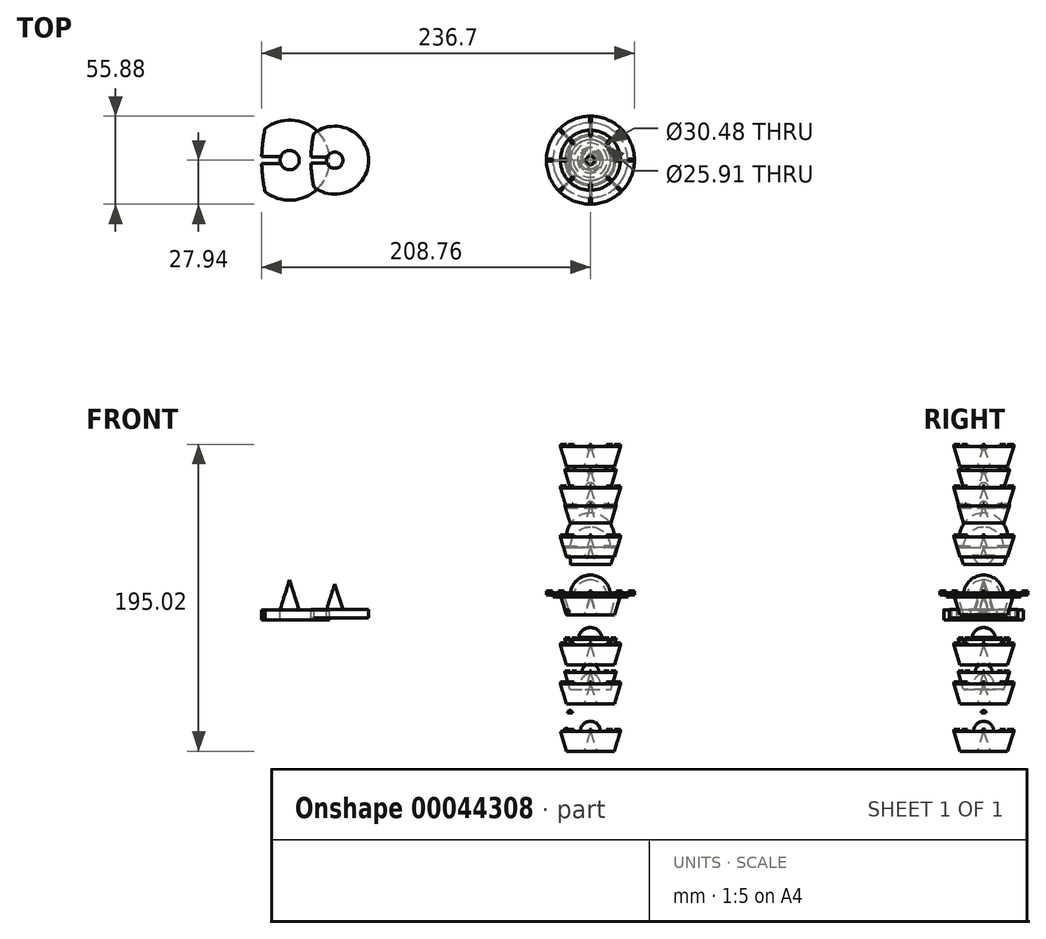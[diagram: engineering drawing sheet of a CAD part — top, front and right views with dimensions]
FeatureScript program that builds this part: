
annotation { "Feature Type Name" : "Feature", "Feature Type Description" : "" }
export const myFeature = defineFeature(function(context is Context, id is Id, definition is map)
    precondition{}
    {
        {
            var Q0;
            Q0=qCreatedBy(makeId("Front.planeOp"),FACE);
            var sketch = newSketch(context, id + "F0", { "sketchPlane" : qUnion([Q0])});
            skLineSegment(sketch, "E0", {"start": v(-19.05, 76.2) * mm, "end": v(0, 76.2) * mm});
            skLineSegment(sketch, "E1", {"start": v(0, 76.2) * mm, "end": v(0, 76.2) * mm});
            skLineSegment(sketch, "E2", {"start": v(-15.24, 63.5) * mm, "end": v(-19.05, 76.2) * mm});
            skLineSegment(sketch, "E3", {"start": v(-15.24, 63.5) * mm, "end": v(-4.06, 63.5) * mm});
            skLineSegment(sketch, "E4", {"start": v(0, 76.2) * mm, "end": v(-4.06, 63.5) * mm});
            skLineSegment(sketch, "E5", {"start": v(-15.24, 63.5) * mm, "end": v(-15.24, 76.2) * mm});
            skLineSegment(sketch, "E6", {"start": v(0, 76.2) * mm, "end": v(0, 79.38) * mm});
            skArc(sketch, "E7", {"start": v(0, 79.38) * mm, "mid": v(-2.25, 78.45) * mm, "end": v(-3.18, 76.2) * mm});
            skSolve(sketch);
        }
        {
            var Q0;
            Q0 = qSketchRegion(id + "F0", true);
            var Q1;
            Q1=sQuery(id+"F0.wireOp",EDGE,"E6");
            revolve(context, id + "F1", {"entities" : qUnion([Q0]), "axis" : qUnion([Q1]), "revolveType" : RevolveType.FULL});
        }
        {
            var Q0;
            Q0=qCreatedBy(makeId("Front.planeOp"),FACE);
            var sketch = newSketch(context, id + "F2", { "sketchPlane" : qUnion([Q0])});
            skLineSegment(sketch, "E8.top", {"start": v(-215.84, 27.03) * mm, "end": v(-190.44, 27.03) * mm});
            skLineSegment(sketch, "E8.left", {"start": v(-215.84, 33.38) * mm, "end": v(-215.84, 27.03) * mm});
            skLineSegment(sketch, "E9", {"start": v(-215.84, 33.38) * mm, "end": v(-190.44, 33.38) * mm});
            skLineSegment(sketch, "E10", {"start": v(-190.44, 33.38) * mm, "end": v(-190.44, 27.03) * mm});
            skLineSegment(sketch, "E11", {"start": v(-190.44, 33.38) * mm, "end": v(-196.53, 33.38) * mm});
            skLineSegment(sketch, "E12", {"start": v(-196.53, 33.38) * mm, "end": v(-190.44, 52.43) * mm});
            skLineSegment(sketch, "E13", {"start": v(-190.44, 52.43) * mm, "end": v(-190.44, 33.38) * mm});
            skSolve(sketch);
        }
        {
            var Q0;
            Q0 = qSketchRegion(id + "F2", true);
            var Q1;
            Q1=sQuery(id+"F2.wireOp",EDGE,"E10");
            revolve(context, id + "F3", {"entities" : qUnion([Q0]), "axis" : qUnion([Q1]), "revolveType" : RevolveType.FULL});
        }
        {
            var Q0;
            Q0=qCreatedBy(makeId("Front.planeOp"),FACE);
            var sketch = newSketch(context, id + "F4", { "sketchPlane" : qUnion([Q0])});
            skLineSegment(sketch, "E14.bottom", {"start": v(-216.4, -1.22) * mm, "end": v(-191, -1.22) * mm});
            skLineSegment(sketch, "E14.top", {"start": v(-216.4, -7.57) * mm, "end": v(-191, -7.57) * mm});
            skLineSegment(sketch, "E14.left", {"start": v(-216.4, -1.22) * mm, "end": v(-216.4, -7.57) * mm});
            skLineSegment(sketch, "E14.right", {"start": v(-191, -1.22) * mm, "end": v(-191, -7.57) * mm});
            skLineSegment(sketch, "E15", {"start": v(-191, -1.22) * mm, "end": v(-191, 17.83) * mm});
            skLineSegment(sketch, "E16", {"start": v(-191, 17.83) * mm, "end": v(-197.1, -1.22) * mm});
            skSolve(sketch);
        }
        {
            var Q0;
            Q0 = qSketchRegion(id + "F4", true);
            var Q1;
            Q1=sQuery(id+"F4.wireOp",EDGE,"E14.right");
            revolve(context, id + "F5", {"entities" : qUnion([Q0]), "axis" : qUnion([Q1]), "revolveType" : RevolveType.FULL});
        }
        {
            var Q0;
            Q0=makeQuery(id+"F3.opRevolve","SWEPT_FACE",FACE,{"disambiguationData":[OSD([sQuery(id+"F2.wireOp",EDGE,"E9")])]});
            var sketch = newSketch(context, id + "F6", { "sketchPlane" : qUnion([Q0])});
            skCircle(sketch, "E17", {"center": v(-114.24, 0) * mm, "radius": 101.6 * mm});
            skCircle(sketch, "E18", {"center": v(-114.24, 0) * mm, "radius": 93.98 * mm});
            skLineSegment(sketch, "E19", {"start": v(-114.24, 0) * mm, "end": v(-201.87, 0) * mm});
            skLineSegment(sketch, "E20.bottom", {"start": v(-214.57, 3.81) * mm, "end": v(-201.87, 3.81) * mm});
            skLineSegment(sketch, "E20.top", {"start": v(-214.57, -3.81) * mm, "end": v(-201.87, -3.81) * mm});
            skLineSegment(sketch, "E20.left", {"start": v(-214.57, 3.81) * mm, "end": v(-214.57, -3.81) * mm});
            skLineSegment(sketch, "E20.right", {"start": v(-201.87, 3.81) * mm, "end": v(-201.87, -3.81) * mm});
            skSolve(sketch);
        }
        {
            var Q0;
            Q0 = qSketchRegion(id + "F6", true);
            var Q1;
            {var subQ4=sQuery(id+"F6.wireOp",EDGE,"E18");var subQ6=sQuery(id+"F6.wireOp",EDGE,"E20.bottom");var subQ7=makeQuery(id+"F6.imprint","INTERSECT",VERTEX,{"derivedFrom":[subQ4,subQ6]});Q1=makeQuery(id+"F6.imprint","IMPRINT",FACE,{"disambiguationData":[TD([[makeQuery(id+"F6.imprint","IMPRINT",EDGE,{"disambiguationData":[TD([[subQ7,-1.0]])],"derivedFrom":subQ4}),1.0]])]});}
            var Q2;
            Q2=makeQuery(id+"F3.opRevolve","SWEPT_FACE",FACE,{"disambiguationData":[OSD([sQuery(id+"F2.wireOp",EDGE,"E8.top")])]});
            extrude(context, id + "F7", {"entities" : qUnion([Q0, Q1]), "operationType" : NewBodyOperationType.REMOVE, "endBound" : BoundingType.UP_TO_SURFACE, "oppositeDirection" : true, "endBoundEntityFace" : qUnion([Q2]), "depth" : 25.4 * mm});
        }
        {
            var Q0;
            Q0=makeQuery(id+"F5.opRevolve","SWEPT_FACE",FACE,{"disambiguationData":[OSD([sQuery(id+"F4.wireOp",EDGE,"E14.bottom")])]});
            var sketch = newSketch(context, id + "F8", { "sketchPlane" : qUnion([Q0])});
            skCircle(sketch, "E21", {"center": v(-114.8, 0) * mm, "radius": 101.6 * mm});
            skCircle(sketch, "E22", {"center": v(-114.8, 0) * mm, "radius": 93.98 * mm});
            skLineSegment(sketch, "E23", {"start": v(-114.8, 0) * mm, "end": v(-197.1, 0) * mm});
            skLineSegment(sketch, "E24.bottom", {"start": v(-214.88, 2.22) * mm, "end": v(-197.1, 2.22) * mm});
            skLineSegment(sketch, "E24.top", {"start": v(-214.88, -2.22) * mm, "end": v(-197.1, -2.22) * mm});
            skLineSegment(sketch, "E24.left", {"start": v(-214.88, 2.22) * mm, "end": v(-214.88, -2.22) * mm});
            skLineSegment(sketch, "E24.right", {"start": v(-197.1, 2.22) * mm, "end": v(-197.1, -2.22) * mm});
            skSolve(sketch);
        }
        {
            var Q0;
            Q0 = qSketchRegion(id + "F8", true);
            var Q1;
            {var subQ4=sQuery(id+"F8.wireOp",EDGE,"E22");var subQ6=sQuery(id+"F8.wireOp",EDGE,"E24.bottom");var subQ7=makeQuery(id+"F8.imprint","INTERSECT",VERTEX,{"derivedFrom":[subQ4,subQ6]});Q1=makeQuery(id+"F8.imprint","IMPRINT",FACE,{"disambiguationData":[TD([[makeQuery(id+"F8.imprint","IMPRINT",EDGE,{"disambiguationData":[TD([[subQ7,-1.0]])],"derivedFrom":subQ4}),1.0]])]});}
            var Q2;
            {var subQ0=sQuery(id+"F8.wireOp",EDGE,"E24.left");Q2=makeQuery(id+"F8.imprint","IMPRINT",FACE,{"disambiguationData":[TD([[makeQuery(id+"F8.imprint","IMPRINT",EDGE,{"derivedFrom":subQ0}),1.0]])]});}
            var Q3;
            Q3=makeQuery(id+"F5.opRevolve","SWEPT_FACE",FACE,{"disambiguationData":[OSD([sQuery(id+"F4.wireOp",EDGE,"E14.top")])]});
            extrude(context, id + "F9", {"entities" : qUnion([Q0, Q1, Q2]), "operationType" : NewBodyOperationType.REMOVE, "endBound" : BoundingType.UP_TO_SURFACE, "oppositeDirection" : true, "endBoundEntityFace" : qUnion([Q3]), "depth" : 25.4 * mm});
        }
        {
            var Q0;
            Q0=qCreatedBy(makeId("Front.planeOp"),FACE);
            var sketch = newSketch(context, id + "F10", { "sketchPlane" : qUnion([Q0])});
            skLineSegment(sketch, "E25", {"start": v(-19.05, 44.92) * mm, "end": v(0, 44.92) * mm});
            skLineSegment(sketch, "E26", {"start": v(0, 44.92) * mm, "end": v(0, 44.92) * mm});
            skLineSegment(sketch, "E27", {"start": v(0, 44.92) * mm, "end": v(-4.06, 32.22) * mm});
            skLineSegment(sketch, "E28", {"start": v(-4.06, 32.22) * mm, "end": v(-15.24, 32.22) * mm});
            skLineSegment(sketch, "E29", {"start": v(-15.24, 32.22) * mm, "end": v(-19.05, 44.92) * mm});
            skLineSegment(sketch, "E30", {"start": v(-15.24, 32.22) * mm, "end": v(-15.24, 44.92) * mm});
            skLineSegment(sketch, "E31", {"start": v(0, 44.92) * mm, "end": v(0, 60.16) * mm});
            skArc(sketch, "E32", {"start": v(0, 60.16) * mm, "mid": v(-10.78, 55.7) * mm, "end": v(-15.24, 44.92) * mm});
            skSolve(sketch);
        }
        {
            var Q0;
            Q0 = qSketchRegion(id + "F10", true);
            var Q1;
            Q1=sQuery(id+"F10.wireOp",EDGE,"E31");
            revolve(context, id + "F11", {"entities" : qUnion([Q0]), "axis" : qUnion([Q1]), "revolveType" : RevolveType.FULL});
        }
        {
            var Q0;
            Q0=qCreatedBy(makeId("Front.planeOp"),FACE);
            var sketch = newSketch(context, id + "F12", { "sketchPlane" : qUnion([Q0])});
            skLineSegment(sketch, "E33", {"start": v(-19.05, 8.07) * mm, "end": v(0, 8.07) * mm});
            skLineSegment(sketch, "E34", {"start": v(0, 8.07) * mm, "end": v(0, 8.07) * mm});
            skLineSegment(sketch, "E35", {"start": v(0, 8.07) * mm, "end": v(-4.06, -4.63) * mm});
            skLineSegment(sketch, "E36", {"start": v(-4.06, -4.63) * mm, "end": v(-15.24, -4.63) * mm});
            skLineSegment(sketch, "E37", {"start": v(-15.24, -4.63) * mm, "end": v(-19.05, 8.07) * mm});
            skLineSegment(sketch, "E38", {"start": v(-15.24, -4.63) * mm, "end": v(-15.24, 8.07) * mm});
            skLineSegment(sketch, "E39", {"start": v(0, 8.07) * mm, "end": v(0, 20.77) * mm});
            skArc(sketch, "E40", {"start": v(0, 20.77) * mm, "mid": v(-8.98, 17.05) * mm, "end": v(-12.7, 8.07) * mm});
            skSolve(sketch);
        }
        {
            var Q0;
            Q0 = qSketchRegion(id + "F12", true);
            var Q1;
            Q1=sQuery(id+"F12.wireOp",EDGE,"E39");
            revolve(context, id + "F13", {"entities" : qUnion([Q0]), "axis" : qUnion([Q1]), "revolveType" : RevolveType.FULL});
        }
        {
            var Q0;
            Q0=qCreatedBy(makeId("Front.planeOp"),FACE);
            var sketch = newSketch(context, id + "F14", { "sketchPlane" : qUnion([Q0])});
            skLineSegment(sketch, "E41.bottom", {"start": v(-27.94, 9.34) * mm, "end": v(-15.24, 9.34) * mm});
            skLineSegment(sketch, "E41.top", {"start": v(-27.94, 8.07) * mm, "end": v(-15.24, 8.07) * mm});
            skLineSegment(sketch, "E41.left", {"start": v(-27.94, 9.34) * mm, "end": v(-27.94, 8.07) * mm});
            skLineSegment(sketch, "E41.right", {"start": v(-15.24, 9.34) * mm, "end": v(-15.24, 8.07) * mm});
            skSolve(sketch);
        }
        {
            var Q0;
            Q0 = qSketchRegion(id + "F14", true);
            var Q1;
            Q1=sQuery(id+"F12.wireOp",EDGE,"E39");
            revolve(context, id + "F15", {"entities" : qUnion([Q0]), "axis" : qUnion([Q1]), "revolveType" : RevolveType.FULL});
        }
        {
            var Q0;
            Q0=qCreatedBy(makeId("Front.planeOp"),FACE);
            var sketch = newSketch(context, id + "F16", { "sketchPlane" : qUnion([Q0])});
            skLineSegment(sketch, "E42", {"start": v(-19.05, -23.63) * mm, "end": v(0, -23.63) * mm});
            skLineSegment(sketch, "E43", {"start": v(0, -23.63) * mm, "end": v(0, -23.63) * mm});
            skLineSegment(sketch, "E44", {"start": v(0, -23.63) * mm, "end": v(-4.06, -36.33) * mm});
            skLineSegment(sketch, "E45", {"start": v(-4.06, -36.33) * mm, "end": v(-15.24, -36.33) * mm});
            skLineSegment(sketch, "E46", {"start": v(-15.24, -36.33) * mm, "end": v(-19.05, -23.63) * mm});
            skLineSegment(sketch, "E47", {"start": v(-15.24, -36.33) * mm, "end": v(-15.24, -23.63) * mm});
            skLineSegment(sketch, "E48", {"start": v(0, -23.63) * mm, "end": v(0, -14.74) * mm});
            skArc(sketch, "E49", {"start": v(0, -14.74) * mm, "mid": v(-6.29, -17.34) * mm, "end": v(-8.9, -23.63) * mm});
            skSolve(sketch);
        }
        {
            var Q0;
            Q0 = qSketchRegion(id + "F16", true);
            var Q1;
            Q1=sQuery(id+"F16.wireOp",EDGE,"E48");
            revolve(context, id + "F17", {"entities" : qUnion([Q0]), "axis" : qUnion([Q1]), "revolveType" : RevolveType.FULL});
        }
        {
            var Q0;
            Q0=qCreatedBy(makeId("Front.planeOp"),FACE);
            var sketch = newSketch(context, id + "F18", { "sketchPlane" : qUnion([Q0])});
            skLineSegment(sketch, "E50", {"start": v(-19.05, -48.33) * mm, "end": v(0, -48.33) * mm});
            skLineSegment(sketch, "E51", {"start": v(0, -48.33) * mm, "end": v(0, -48.33) * mm});
            skLineSegment(sketch, "E52", {"start": v(0, -48.33) * mm, "end": v(-4.06, -61.03) * mm});
            skLineSegment(sketch, "E53", {"start": v(-4.06, -61.03) * mm, "end": v(-15.24, -61.03) * mm});
            skLineSegment(sketch, "E54", {"start": v(-15.24, -61.03) * mm, "end": v(-19.05, -48.33) * mm});
            skLineSegment(sketch, "E55", {"start": v(-15.24, -61.03) * mm, "end": v(-15.24, -48.33) * mm});
            skLineSegment(sketch, "E56", {"start": v(0, -48.33) * mm, "end": v(0, -41.98) * mm});
            skArc(sketch, "E57", {"start": v(0, -41.98) * mm, "mid": v(-4.5, -43.84) * mm, "end": v(-6.35, -48.33) * mm});
            skSolve(sketch);
        }
        {
            var Q0;
            Q0 = qSketchRegion(id + "F18", true);
            var Q1;
            Q1=sQuery(id+"F18.wireOp",EDGE,"E56");
            revolve(context, id + "F19", {"entities" : qUnion([Q0]), "axis" : qUnion([Q1]), "revolveType" : RevolveType.FULL});
        }
        {
            var Q0;
            Q0=qCreatedBy(makeId("Front.planeOp"),FACE);
            var sketch = newSketch(context, id + "F20", { "sketchPlane" : qUnion([Q0])});
            skLineSegment(sketch, "E58", {"start": v(-19.05, -78.45) * mm, "end": v(0, -78.45) * mm});
            skLineSegment(sketch, "E59", {"start": v(0, -78.45) * mm, "end": v(0, -78.45) * mm});
            skLineSegment(sketch, "E60", {"start": v(0, -78.45) * mm, "end": v(-4.06, -91.15) * mm});
            skLineSegment(sketch, "E61", {"start": v(-4.06, -91.15) * mm, "end": v(-15.24, -91.15) * mm});
            skLineSegment(sketch, "E62", {"start": v(-15.24, -91.15) * mm, "end": v(-19.05, -78.45) * mm});
            skLineSegment(sketch, "E63", {"start": v(-15.24, -91.15) * mm, "end": v(-15.24, -78.45) * mm});
            skLineSegment(sketch, "E64", {"start": v(0, -78.45) * mm, "end": v(0, -72.1) * mm});
            skArc(sketch, "E65", {"start": v(0, -72.1) * mm, "mid": v(-4.5, -73.96) * mm, "end": v(-6.35, -78.45) * mm});
            skSolve(sketch);
        }
        {
            var Q0;
            Q0 = qSketchRegion(id + "F20", true);
            var Q1;
            Q1=sQuery(id+"F20.wireOp",EDGE,"E64");
            revolve(context, id + "F21", {"entities" : qUnion([Q0]), "axis" : qUnion([Q1]), "revolveType" : RevolveType.FULL});
        }
        {
            var Q0;
            Q0=qCreatedBy(makeId("Front.planeOp"),FACE);
            var sketch = newSketch(context, id + "F22", { "sketchPlane" : qUnion([Q0])});
            skLineSegment(sketch, "E66", {"start": v(-15.24, -78.45) * mm, "end": v(-15.24, -76.67) * mm});
            skArc(sketch, "E67", {"start": v(-15.24, -76.67) * mm, "mid": v(-16.5, -77.2) * mm, "end": v(-17.02, -78.45) * mm});
            skLineSegment(sketch, "E68", {"start": v(-17.02, -78.45) * mm, "end": v(-15.24, -78.45) * mm});
            skSolve(sketch);
        }
        {
            var Q0;
            Q0 = qSketchRegion(id + "F22", true);
            var Q1;
            Q1=sQuery(id+"F22.wireOp",EDGE,"E66");
            revolve(context, id + "F23", {"entities" : qUnion([Q0]), "axis" : qUnion([Q1]), "revolveType" : RevolveType.FULL});
        }
        {
            var Q0;
            Q0=qCreatedBy(makeId("Front.planeOp"),FACE);
            var sketch = newSketch(context, id + "F24", { "sketchPlane" : qUnion([Q0])});
            skLineSegment(sketch, "E69", {"start": v(-19.05, 102.6) * mm, "end": v(0, 102.6) * mm});
            skLineSegment(sketch, "E70", {"start": v(0, 102.6) * mm, "end": v(0, 102.6) * mm});
            skLineSegment(sketch, "E71", {"start": v(0, 102.6) * mm, "end": v(-4.06, 89.9) * mm});
            skLineSegment(sketch, "E72", {"start": v(-4.06, 89.9) * mm, "end": v(-15.24, 89.9) * mm});
            skLineSegment(sketch, "E73", {"start": v(-15.24, 89.9) * mm, "end": v(-19.05, 102.6) * mm});
            skLineSegment(sketch, "E74", {"start": v(-15.24, 89.9) * mm, "end": v(-15.24, 102.6) * mm});
            skLineSegment(sketch, "E75", {"start": v(0, 102.6) * mm, "end": v(0, 105.14) * mm});
            skArc(sketch, "E76", {"start": v(0, 105.14) * mm, "mid": v(-1.83, 104.43) * mm, "end": v(-2.54, 102.6) * mm});
            skSolve(sketch);
        }
        {
            var Q0;
            Q0 = qSketchRegion(id + "F24", true);
            var Q1;
            Q1=sQuery(id+"F24.wireOp",EDGE,"E75");
            revolve(context, id + "F25", {"entities" : qUnion([Q0]), "axis" : qUnion([Q1]), "revolveType" : RevolveType.FULL});
        }
        {
            var Q0;
            Q0=qCreatedBy(makeId("Top.planeOp"),FACE);
            var sketch = newSketch(context, id + "F26", { "sketchPlane" : qUnion([Q0])});
            skLineSegment(sketch, "E77", {"start": v(0, 19.05) * mm, "end": v(0, 0) * mm});
            skLineSegment(sketch, "E78", {"start": v(0, 0) * mm, "end": v(0, -19.05) * mm});
            skLineSegment(sketch, "E79", {"start": v(0, 0) * mm, "end": v(19.05, 0) * mm});
            skLineSegment(sketch, "E80", {"start": v(0, 0) * mm, "end": v(-19.05, 0) * mm});
            skLineSegment(sketch, "E81", {"start": v(-19.05, 0) * mm, "end": v(0, 19.05) * mm});
            skLineSegment(sketch, "E82", {"start": v(0, 19.05) * mm, "end": v(19.05, 0) * mm});
            skLineSegment(sketch, "E83", {"start": v(19.05, 0) * mm, "end": v(0, -19.05) * mm});
            skLineSegment(sketch, "E84", {"start": v(0, -19.05) * mm, "end": v(-19.05, 0) * mm});
            skLineSegment(sketch, "E85", {"start": v(0, 0) * mm, "end": v(-9.52, 9.52) * mm});
            skLineSegment(sketch, "E86", {"start": v(0, 0) * mm, "end": v(9.52, 9.52) * mm});
            skLineSegment(sketch, "E87", {"start": v(0, 0) * mm, "end": v(9.53, -9.52) * mm});
            skLineSegment(sketch, "E88", {"start": v(0, 0) * mm, "end": v(-9.53, -9.53) * mm});
            skLineSegment(sketch, "E89", {"start": v(0, 0) * mm, "end": v(-13.47, 13.47) * mm});
            skLineSegment(sketch, "E90", {"start": v(0, 0) * mm, "end": v(13.47, 13.47) * mm});
            skLineSegment(sketch, "E91", {"start": v(0, 0) * mm, "end": v(13.47, -13.47) * mm});
            skLineSegment(sketch, "E92", {"start": v(0, 0) * mm, "end": v(-13.47, -13.47) * mm});
            skLineSegment(sketch, "E93", {"start": v(0, 0) * mm, "end": v(0, 27.94) * mm});
            skLineSegment(sketch, "E94", {"start": v(0, 0) * mm, "end": v(19.76, 19.76) * mm});
            skLineSegment(sketch, "E95", {"start": v(0, 0) * mm, "end": v(27.94, 0) * mm});
            skLineSegment(sketch, "E96", {"start": v(0, 0) * mm, "end": v(19.76, -19.76) * mm});
            skLineSegment(sketch, "E97", {"start": v(0, 0) * mm, "end": v(0, -27.94) * mm});
            skLineSegment(sketch, "E98", {"start": v(0, 0) * mm, "end": v(-19.76, -19.76) * mm});
            skLineSegment(sketch, "E99", {"start": v(0, 0) * mm, "end": v(-27.94, 0) * mm});
            skLineSegment(sketch, "E100", {"start": v(0, 0) * mm, "end": v(-19.76, 19.76) * mm});
            skLineSegment(sketch, "E101", {"start": v(0, 0) * mm, "end": v(0, -4.32) * mm});
            skSolve(sketch);
        }
        {
            var Q0;
            Q0=makeQuery(id+"F1.opRevolve","SWEPT_FACE",FACE,{"disambiguationData":[OSD([sQuery(id+"F0.wireOp",EDGE,"E0")])]});
            var sketch = newSketch(context, id + "F27", { "sketchPlane" : qUnion([Q0])});
            skLineSegment(sketch, "E102.bottom", {"start": v(-13.92, 13.02) * mm, "end": v(-13.02, 13.92) * mm});
            skLineSegment(sketch, "E102.top", {"start": v(-11.23, 10.33) * mm, "end": v(-10.33, 11.23) * mm});
            skLineSegment(sketch, "E102.left", {"start": v(-13.92, 13.02) * mm, "end": v(-11.23, 10.33) * mm});
            skLineSegment(sketch, "E102.right", {"start": v(-13.02, 13.92) * mm, "end": v(-10.33, 11.23) * mm});
            skLineSegment(sketch, "E103.bottom", {"start": v(-0.63, 19.05) * mm, "end": v(0.63, 19.05) * mm});
            skLineSegment(sketch, "E103.top", {"start": v(-0.64, 15.24) * mm, "end": v(0.64, 15.24) * mm});
            skLineSegment(sketch, "E103.left", {"start": v(-0.64, 19.05) * mm, "end": v(-0.64, 15.24) * mm});
            skLineSegment(sketch, "E103.right", {"start": v(0.64, 19.05) * mm, "end": v(0.64, 15.24) * mm});
            skLineSegment(sketch, "E104.bottom", {"start": v(13.02, 13.92) * mm, "end": v(13.92, 13.02) * mm});
            skLineSegment(sketch, "E104.top", {"start": v(10.33, 11.23) * mm, "end": v(11.23, 10.33) * mm});
            skLineSegment(sketch, "E104.left", {"start": v(13.02, 13.92) * mm, "end": v(10.33, 11.23) * mm});
            skLineSegment(sketch, "E104.right", {"start": v(13.92, 13.02) * mm, "end": v(11.23, 10.33) * mm});
            skLineSegment(sketch, "E105.bottom", {"start": v(15.24, -0.64) * mm, "end": v(15.24, 0.64) * mm});
            skLineSegment(sketch, "E105.top", {"start": v(19.05, -0.64) * mm, "end": v(19.05, 0.64) * mm});
            skLineSegment(sketch, "E105.left", {"start": v(15.24, 0.64) * mm, "end": v(19.05, 0.64) * mm});
            skLineSegment(sketch, "E105.right", {"start": v(15.24, -0.64) * mm, "end": v(19.05, -0.64) * mm});
            skLineSegment(sketch, "E106.bottom", {"start": v(13.02, -13.92) * mm, "end": v(13.92, -13.02) * mm});
            skLineSegment(sketch, "E106.top", {"start": v(10.33, -11.23) * mm, "end": v(11.23, -10.33) * mm});
            skLineSegment(sketch, "E106.left", {"start": v(13.92, -13.02) * mm, "end": v(11.23, -10.33) * mm});
            skLineSegment(sketch, "E106.right", {"start": v(13.02, -13.92) * mm, "end": v(10.33, -11.23) * mm});
            skLineSegment(sketch, "E107.bottom", {"start": v(-0.64, -15.24) * mm, "end": v(0.64, -15.24) * mm});
            skLineSegment(sketch, "E107.top", {"start": v(-0.64, -19.05) * mm, "end": v(0.64, -19.05) * mm});
            skLineSegment(sketch, "E107.left", {"start": v(-0.64, -15.24) * mm, "end": v(-0.64, -19.05) * mm});
            skLineSegment(sketch, "E107.right", {"start": v(0.64, -15.24) * mm, "end": v(0.64, -19.05) * mm});
            skLineSegment(sketch, "E108.bottom", {"start": v(-11.23, -10.33) * mm, "end": v(-10.33, -11.23) * mm});
            skLineSegment(sketch, "E108.top", {"start": v(-13.92, -13.02) * mm, "end": v(-13.02, -13.92) * mm});
            skLineSegment(sketch, "E108.left", {"start": v(-11.23, -10.33) * mm, "end": v(-13.92, -13.02) * mm});
            skLineSegment(sketch, "E108.right", {"start": v(-10.33, -11.23) * mm, "end": v(-13.02, -13.92) * mm});
            skLineSegment(sketch, "E109.bottom", {"start": v(-19.05, 0.63) * mm, "end": v(-15.24, 0.63) * mm});
            skLineSegment(sketch, "E109.top", {"start": v(-19.05, -0.64) * mm, "end": v(-15.24, -0.64) * mm});
            skLineSegment(sketch, "E109.left", {"start": v(-19.05, 0.64) * mm, "end": v(-19.05, -0.64) * mm});
            skLineSegment(sketch, "E109.right", {"start": v(-15.24, 0.63) * mm, "end": v(-15.24, -0.63) * mm});
            skSolve(sketch);
        }
        {
            var Q0;
            Q0 = qSketchRegion(id + "F27", true);
            extrude(context, id + "F28", {"entities" : qUnion([Q0]), "operationType" : NewBodyOperationType.ADD, "depth" : 1.27 * mm});
        }
        {
            var Q0;
            Q0=makeQuery(id+"F11.opRevolve","SWEPT_FACE",FACE,{"disambiguationData":[OSD([sQuery(id+"F10.wireOp",EDGE,"E25")])]});
            var sketch = newSketch(context, id + "F29", { "sketchPlane" : qUnion([Q0])});
            skLineSegment(sketch, "E110.bottom", {"start": v(-13.92, 13.02) * mm, "end": v(-13.02, 13.92) * mm});
            skLineSegment(sketch, "E110.top", {"start": v(-11.23, 10.33) * mm, "end": v(-10.33, 11.23) * mm});
            skLineSegment(sketch, "E110.left", {"start": v(-13.92, 13.02) * mm, "end": v(-11.23, 10.33) * mm});
            skLineSegment(sketch, "E110.right", {"start": v(-13.02, 13.92) * mm, "end": v(-10.33, 11.23) * mm});
            skLineSegment(sketch, "E111.bottom", {"start": v(-0.64, 19.05) * mm, "end": v(0.63, 19.05) * mm});
            skLineSegment(sketch, "E111.top", {"start": v(-0.64, 15.24) * mm, "end": v(0.63, 15.24) * mm});
            skLineSegment(sketch, "E111.left", {"start": v(-0.64, 19.05) * mm, "end": v(-0.64, 15.24) * mm});
            skLineSegment(sketch, "E111.right", {"start": v(0.63, 19.05) * mm, "end": v(0.63, 15.24) * mm});
            skLineSegment(sketch, "E112.bottom", {"start": v(13.02, 13.92) * mm, "end": v(13.92, 13.02) * mm});
            skLineSegment(sketch, "E112.top", {"start": v(10.33, 11.23) * mm, "end": v(11.23, 10.33) * mm});
            skLineSegment(sketch, "E112.left", {"start": v(13.02, 13.92) * mm, "end": v(10.33, 11.23) * mm});
            skLineSegment(sketch, "E112.right", {"start": v(13.92, 13.02) * mm, "end": v(11.23, 10.33) * mm});
            skLineSegment(sketch, "E113.bottom", {"start": v(15.24, -0.63) * mm, "end": v(15.24, 0.64) * mm});
            skLineSegment(sketch, "E113.top", {"start": v(19.05, -0.63) * mm, "end": v(19.05, 0.64) * mm});
            skLineSegment(sketch, "E113.left", {"start": v(15.24, 0.64) * mm, "end": v(19.05, 0.64) * mm});
            skLineSegment(sketch, "E113.right", {"start": v(15.24, -0.63) * mm, "end": v(19.05, -0.63) * mm});
            skLineSegment(sketch, "E114.bottom", {"start": v(13.02, -13.92) * mm, "end": v(13.92, -13.02) * mm});
            skLineSegment(sketch, "E114.top", {"start": v(10.33, -11.23) * mm, "end": v(11.23, -10.33) * mm});
            skLineSegment(sketch, "E114.left", {"start": v(13.92, -13.02) * mm, "end": v(11.23, -10.33) * mm});
            skLineSegment(sketch, "E114.right", {"start": v(13.02, -13.92) * mm, "end": v(10.33, -11.23) * mm});
            skLineSegment(sketch, "E115.bottom", {"start": v(-0.63, -15.24) * mm, "end": v(0.63, -15.24) * mm});
            skLineSegment(sketch, "E115.top", {"start": v(-0.64, -19.05) * mm, "end": v(0.64, -19.05) * mm});
            skLineSegment(sketch, "E115.left", {"start": v(-0.63, -15.24) * mm, "end": v(-0.63, -19.05) * mm});
            skLineSegment(sketch, "E115.right", {"start": v(0.64, -15.24) * mm, "end": v(0.64, -19.05) * mm});
            skLineSegment(sketch, "E116.bottom", {"start": v(-11.23, -10.33) * mm, "end": v(-10.33, -11.23) * mm});
            skLineSegment(sketch, "E116.top", {"start": v(-13.92, -13.02) * mm, "end": v(-13.02, -13.92) * mm});
            skLineSegment(sketch, "E116.left", {"start": v(-11.23, -10.33) * mm, "end": v(-13.92, -13.02) * mm});
            skLineSegment(sketch, "E116.right", {"start": v(-10.33, -11.23) * mm, "end": v(-13.02, -13.92) * mm});
            skLineSegment(sketch, "E117.bottom", {"start": v(-19.05, 0.63) * mm, "end": v(-15.24, 0.63) * mm});
            skLineSegment(sketch, "E117.top", {"start": v(-19.05, -0.63) * mm, "end": v(-15.24, -0.63) * mm});
            skLineSegment(sketch, "E117.left", {"start": v(-19.05, 0.64) * mm, "end": v(-19.05, -0.64) * mm});
            skLineSegment(sketch, "E117.right", {"start": v(-15.24, 0.63) * mm, "end": v(-15.24, -0.63) * mm});
            skSolve(sketch);
        }
        {
            var Q0;
            Q0 = qSketchRegion(id + "F29", true);
            extrude(context, id + "F30", {"entities" : qUnion([Q0]), "operationType" : NewBodyOperationType.ADD, "depth" : 1.27 * mm});
        }
        {
            var Q0;
            Q0=makeQuery(id+"F17.opRevolve","SWEPT_FACE",FACE,{"disambiguationData":[OSD([sQuery(id+"F16.wireOp",EDGE,"E42")])]});
            var sketch = newSketch(context, id + "F31", { "sketchPlane" : qUnion([Q0])});
            skLineSegment(sketch, "E118.bottom", {"start": v(-13.92, 13.02) * mm, "end": v(-13.02, 13.92) * mm});
            skLineSegment(sketch, "E118.top", {"start": v(-11.23, 10.33) * mm, "end": v(-10.33, 11.23) * mm});
            skLineSegment(sketch, "E118.left", {"start": v(-13.92, 13.02) * mm, "end": v(-11.23, 10.33) * mm});
            skLineSegment(sketch, "E118.right", {"start": v(-13.02, 13.92) * mm, "end": v(-10.33, 11.23) * mm});
            skLineSegment(sketch, "E119.bottom", {"start": v(-0.64, 19.05) * mm, "end": v(0.63, 19.05) * mm});
            skLineSegment(sketch, "E119.top", {"start": v(-0.64, 15.24) * mm, "end": v(0.63, 15.24) * mm});
            skLineSegment(sketch, "E119.left", {"start": v(-0.64, 19.05) * mm, "end": v(-0.64, 15.24) * mm});
            skLineSegment(sketch, "E119.right", {"start": v(0.63, 19.05) * mm, "end": v(0.63, 15.24) * mm});
            skLineSegment(sketch, "E120.bottom", {"start": v(13.02, 13.92) * mm, "end": v(13.92, 13.02) * mm});
            skLineSegment(sketch, "E120.top", {"start": v(10.33, 11.23) * mm, "end": v(11.23, 10.33) * mm});
            skLineSegment(sketch, "E120.left", {"start": v(13.02, 13.92) * mm, "end": v(10.33, 11.23) * mm});
            skLineSegment(sketch, "E120.right", {"start": v(13.92, 13.02) * mm, "end": v(11.23, 10.33) * mm});
            skLineSegment(sketch, "E121.bottom", {"start": v(15.24, -0.63) * mm, "end": v(15.24, 0.64) * mm});
            skLineSegment(sketch, "E121.top", {"start": v(19.05, -0.63) * mm, "end": v(19.05, 0.64) * mm});
            skLineSegment(sketch, "E121.left", {"start": v(15.24, 0.64) * mm, "end": v(19.05, 0.64) * mm});
            skLineSegment(sketch, "E121.right", {"start": v(15.24, -0.63) * mm, "end": v(19.05, -0.63) * mm});
            skLineSegment(sketch, "E122.bottom", {"start": v(13.02, -13.92) * mm, "end": v(13.92, -13.02) * mm});
            skLineSegment(sketch, "E122.top", {"start": v(10.33, -11.23) * mm, "end": v(11.23, -10.33) * mm});
            skLineSegment(sketch, "E122.left", {"start": v(13.92, -13.02) * mm, "end": v(11.23, -10.33) * mm});
            skLineSegment(sketch, "E122.right", {"start": v(13.02, -13.92) * mm, "end": v(10.33, -11.23) * mm});
            skLineSegment(sketch, "E123.bottom", {"start": v(-0.63, -15.24) * mm, "end": v(0.63, -15.24) * mm});
            skLineSegment(sketch, "E123.top", {"start": v(-0.64, -19.05) * mm, "end": v(0.64, -19.05) * mm});
            skLineSegment(sketch, "E123.left", {"start": v(-0.63, -15.24) * mm, "end": v(-0.63, -19.05) * mm});
            skLineSegment(sketch, "E123.right", {"start": v(0.64, -15.24) * mm, "end": v(0.64, -19.05) * mm});
            skLineSegment(sketch, "E124.bottom", {"start": v(-11.23, -10.33) * mm, "end": v(-10.33, -11.23) * mm});
            skLineSegment(sketch, "E124.top", {"start": v(-13.92, -13.02) * mm, "end": v(-13.02, -13.92) * mm});
            skLineSegment(sketch, "E124.left", {"start": v(-11.23, -10.33) * mm, "end": v(-13.92, -13.02) * mm});
            skLineSegment(sketch, "E124.right", {"start": v(-10.33, -11.23) * mm, "end": v(-13.02, -13.92) * mm});
            skLineSegment(sketch, "E125.bottom", {"start": v(-19.05, 0.63) * mm, "end": v(-15.24, 0.63) * mm});
            skLineSegment(sketch, "E125.top", {"start": v(-19.05, -0.63) * mm, "end": v(-15.24, -0.63) * mm});
            skLineSegment(sketch, "E125.left", {"start": v(-19.05, 0.64) * mm, "end": v(-19.05, -0.64) * mm});
            skLineSegment(sketch, "E125.right", {"start": v(-15.24, 0.63) * mm, "end": v(-15.24, -0.63) * mm});
            skSolve(sketch);
        }
        {
            var Q0;
            Q0 = qSketchRegion(id + "F31", true);
            extrude(context, id + "F32", {"entities" : qUnion([Q0]), "operationType" : NewBodyOperationType.ADD, "depth" : 1.27 * mm});
        }
        {
            var Q0;
            Q0=makeQuery(id+"F19.opRevolve","SWEPT_FACE",FACE,{"disambiguationData":[OSD([sQuery(id+"F18.wireOp",EDGE,"E50")])]});
            var sketch = newSketch(context, id + "F33", { "sketchPlane" : qUnion([Q0])});
            skLineSegment(sketch, "E126.bottom", {"start": v(-13.92, 13.02) * mm, "end": v(-13.02, 13.92) * mm});
            skLineSegment(sketch, "E126.top", {"start": v(-11.23, 10.33) * mm, "end": v(-10.33, 11.23) * mm});
            skLineSegment(sketch, "E126.left", {"start": v(-13.92, 13.02) * mm, "end": v(-11.23, 10.33) * mm});
            skLineSegment(sketch, "E126.right", {"start": v(-13.02, 13.92) * mm, "end": v(-10.33, 11.23) * mm});
            skLineSegment(sketch, "E127.bottom", {"start": v(-0.64, 19.05) * mm, "end": v(0.63, 19.05) * mm});
            skLineSegment(sketch, "E127.top", {"start": v(-0.64, 15.24) * mm, "end": v(0.63, 15.24) * mm});
            skLineSegment(sketch, "E127.left", {"start": v(-0.64, 19.05) * mm, "end": v(-0.64, 15.24) * mm});
            skLineSegment(sketch, "E127.right", {"start": v(0.63, 19.05) * mm, "end": v(0.63, 15.24) * mm});
            skLineSegment(sketch, "E128.bottom", {"start": v(13.02, 13.92) * mm, "end": v(13.92, 13.02) * mm});
            skLineSegment(sketch, "E128.top", {"start": v(10.33, 11.23) * mm, "end": v(11.23, 10.33) * mm});
            skLineSegment(sketch, "E128.left", {"start": v(13.02, 13.92) * mm, "end": v(10.33, 11.23) * mm});
            skLineSegment(sketch, "E128.right", {"start": v(13.92, 13.02) * mm, "end": v(11.23, 10.33) * mm});
            skLineSegment(sketch, "E129.bottom", {"start": v(15.24, -0.63) * mm, "end": v(15.24, 0.64) * mm});
            skLineSegment(sketch, "E129.top", {"start": v(19.05, -0.63) * mm, "end": v(19.05, 0.64) * mm});
            skLineSegment(sketch, "E129.left", {"start": v(15.24, 0.64) * mm, "end": v(19.05, 0.64) * mm});
            skLineSegment(sketch, "E129.right", {"start": v(15.24, -0.63) * mm, "end": v(19.05, -0.63) * mm});
            skLineSegment(sketch, "E130.bottom", {"start": v(13.02, -13.92) * mm, "end": v(13.92, -13.02) * mm});
            skLineSegment(sketch, "E130.top", {"start": v(10.33, -11.23) * mm, "end": v(11.23, -10.33) * mm});
            skLineSegment(sketch, "E130.left", {"start": v(13.92, -13.02) * mm, "end": v(11.23, -10.33) * mm});
            skLineSegment(sketch, "E130.right", {"start": v(13.02, -13.92) * mm, "end": v(10.33, -11.23) * mm});
            skLineSegment(sketch, "E131.bottom", {"start": v(-0.63, -15.24) * mm, "end": v(0.63, -15.24) * mm});
            skLineSegment(sketch, "E131.top", {"start": v(-0.64, -19.05) * mm, "end": v(0.64, -19.05) * mm});
            skLineSegment(sketch, "E131.left", {"start": v(-0.63, -15.24) * mm, "end": v(-0.63, -19.05) * mm});
            skLineSegment(sketch, "E131.right", {"start": v(0.64, -15.24) * mm, "end": v(0.64, -19.05) * mm});
            skLineSegment(sketch, "E132.bottom", {"start": v(-11.23, -10.33) * mm, "end": v(-10.33, -11.23) * mm});
            skLineSegment(sketch, "E132.top", {"start": v(-13.92, -13.02) * mm, "end": v(-13.02, -13.92) * mm});
            skLineSegment(sketch, "E132.left", {"start": v(-11.23, -10.33) * mm, "end": v(-13.92, -13.02) * mm});
            skLineSegment(sketch, "E132.right", {"start": v(-10.33, -11.23) * mm, "end": v(-13.02, -13.92) * mm});
            skLineSegment(sketch, "E133.bottom", {"start": v(-19.05, 0.63) * mm, "end": v(-15.24, 0.63) * mm});
            skLineSegment(sketch, "E133.top", {"start": v(-19.05, -0.63) * mm, "end": v(-15.24, -0.63) * mm});
            skLineSegment(sketch, "E133.left", {"start": v(-19.05, 0.64) * mm, "end": v(-19.05, -0.64) * mm});
            skLineSegment(sketch, "E133.right", {"start": v(-15.24, 0.63) * mm, "end": v(-15.24, -0.63) * mm});
            skSolve(sketch);
        }
        {
            var Q0;
            Q0 = qSketchRegion(id + "F33", true);
            extrude(context, id + "F34", {"entities" : qUnion([Q0]), "operationType" : NewBodyOperationType.ADD, "depth" : 1.27 * mm});
        }
        {
            var Q0;
            Q0=makeQuery(id+"F25.opRevolve","SWEPT_FACE",FACE,{"disambiguationData":[OSD([sQuery(id+"F24.wireOp",EDGE,"E69")])]});
            var sketch = newSketch(context, id + "F35", { "sketchPlane" : qUnion([Q0])});
            skLineSegment(sketch, "E134.bottom", {"start": v(-13.92, 13.02) * mm, "end": v(-13.02, 13.92) * mm});
            skLineSegment(sketch, "E134.top", {"start": v(-11.23, 10.33) * mm, "end": v(-10.33, 11.23) * mm});
            skLineSegment(sketch, "E134.left", {"start": v(-13.92, 13.02) * mm, "end": v(-11.23, 10.33) * mm});
            skLineSegment(sketch, "E134.right", {"start": v(-13.02, 13.92) * mm, "end": v(-10.33, 11.23) * mm});
            skLineSegment(sketch, "E135.bottom", {"start": v(-0.64, 19.05) * mm, "end": v(0.63, 19.05) * mm});
            skLineSegment(sketch, "E135.top", {"start": v(-0.64, 15.24) * mm, "end": v(0.63, 15.24) * mm});
            skLineSegment(sketch, "E135.left", {"start": v(-0.64, 19.05) * mm, "end": v(-0.64, 15.24) * mm});
            skLineSegment(sketch, "E135.right", {"start": v(0.63, 19.05) * mm, "end": v(0.63, 15.24) * mm});
            skLineSegment(sketch, "E136.bottom", {"start": v(13.02, 13.92) * mm, "end": v(13.92, 13.02) * mm});
            skLineSegment(sketch, "E136.top", {"start": v(10.33, 11.23) * mm, "end": v(11.23, 10.33) * mm});
            skLineSegment(sketch, "E136.left", {"start": v(13.02, 13.92) * mm, "end": v(10.33, 11.23) * mm});
            skLineSegment(sketch, "E136.right", {"start": v(13.92, 13.02) * mm, "end": v(11.23, 10.33) * mm});
            skLineSegment(sketch, "E137.bottom", {"start": v(15.24, -0.63) * mm, "end": v(15.24, 0.64) * mm});
            skLineSegment(sketch, "E137.top", {"start": v(19.05, -0.63) * mm, "end": v(19.05, 0.64) * mm});
            skLineSegment(sketch, "E137.left", {"start": v(15.24, 0.64) * mm, "end": v(19.05, 0.64) * mm});
            skLineSegment(sketch, "E137.right", {"start": v(15.24, -0.63) * mm, "end": v(19.05, -0.63) * mm});
            skLineSegment(sketch, "E138.bottom", {"start": v(13.02, -13.92) * mm, "end": v(13.92, -13.02) * mm});
            skLineSegment(sketch, "E138.top", {"start": v(10.33, -11.23) * mm, "end": v(11.23, -10.33) * mm});
            skLineSegment(sketch, "E138.left", {"start": v(13.92, -13.02) * mm, "end": v(11.23, -10.33) * mm});
            skLineSegment(sketch, "E138.right", {"start": v(13.02, -13.92) * mm, "end": v(10.33, -11.23) * mm});
            skLineSegment(sketch, "E139.bottom", {"start": v(-0.63, -15.24) * mm, "end": v(0.63, -15.24) * mm});
            skLineSegment(sketch, "E139.top", {"start": v(-0.64, -19.05) * mm, "end": v(0.64, -19.05) * mm});
            skLineSegment(sketch, "E139.left", {"start": v(-0.63, -15.24) * mm, "end": v(-0.63, -19.05) * mm});
            skLineSegment(sketch, "E139.right", {"start": v(0.64, -15.24) * mm, "end": v(0.64, -19.05) * mm});
            skLineSegment(sketch, "E140.bottom", {"start": v(-11.23, -10.33) * mm, "end": v(-10.33, -11.23) * mm});
            skLineSegment(sketch, "E140.top", {"start": v(-13.92, -13.02) * mm, "end": v(-13.02, -13.92) * mm});
            skLineSegment(sketch, "E140.left", {"start": v(-11.23, -10.33) * mm, "end": v(-13.92, -13.02) * mm});
            skLineSegment(sketch, "E140.right", {"start": v(-10.33, -11.23) * mm, "end": v(-13.02, -13.92) * mm});
            skLineSegment(sketch, "E141.bottom", {"start": v(-19.05, 0.63) * mm, "end": v(-15.24, 0.63) * mm});
            skLineSegment(sketch, "E141.top", {"start": v(-19.05, -0.63) * mm, "end": v(-15.24, -0.63) * mm});
            skLineSegment(sketch, "E141.left", {"start": v(-19.05, 0.64) * mm, "end": v(-19.05, -0.64) * mm});
            skLineSegment(sketch, "E141.right", {"start": v(-15.24, 0.63) * mm, "end": v(-15.24, -0.63) * mm});
            skSolve(sketch);
        }
        {
            var Q0;
            Q0 = qSketchRegion(id + "F35", true);
            extrude(context, id + "F36", {"entities" : qUnion([Q0]), "operationType" : NewBodyOperationType.ADD, "depth" : 1.27 * mm});
        }
        {
            var Q0;
            Q0=makeQuery(id+"F21.opRevolve","SWEPT_FACE",FACE,{"disambiguationData":[OSD([sQuery(id+"F20.wireOp",EDGE,"E58")])]});
            var sketch = newSketch(context, id + "F37", { "sketchPlane" : qUnion([Q0])});
            skLineSegment(sketch, "E142.bottom", {"start": v(-13.92, 13.02) * mm, "end": v(-13.02, 13.92) * mm});
            skLineSegment(sketch, "E142.top", {"start": v(-11.23, 10.33) * mm, "end": v(-10.33, 11.23) * mm});
            skLineSegment(sketch, "E142.left", {"start": v(-13.92, 13.02) * mm, "end": v(-11.23, 10.33) * mm});
            skLineSegment(sketch, "E142.right", {"start": v(-13.02, 13.92) * mm, "end": v(-10.33, 11.23) * mm});
            skLineSegment(sketch, "E143.bottom", {"start": v(-0.64, 19.05) * mm, "end": v(0.63, 19.05) * mm});
            skLineSegment(sketch, "E143.top", {"start": v(-0.64, 15.24) * mm, "end": v(0.63, 15.24) * mm});
            skLineSegment(sketch, "E143.left", {"start": v(-0.64, 19.05) * mm, "end": v(-0.64, 15.24) * mm});
            skLineSegment(sketch, "E143.right", {"start": v(0.63, 19.05) * mm, "end": v(0.63, 15.24) * mm});
            skLineSegment(sketch, "E144.bottom", {"start": v(13.02, 13.92) * mm, "end": v(13.92, 13.02) * mm});
            skLineSegment(sketch, "E144.top", {"start": v(10.33, 11.23) * mm, "end": v(11.23, 10.33) * mm});
            skLineSegment(sketch, "E144.left", {"start": v(13.02, 13.92) * mm, "end": v(10.33, 11.23) * mm});
            skLineSegment(sketch, "E144.right", {"start": v(13.92, 13.02) * mm, "end": v(11.23, 10.33) * mm});
            skLineSegment(sketch, "E145.bottom", {"start": v(15.24, -0.63) * mm, "end": v(15.24, 0.64) * mm});
            skLineSegment(sketch, "E145.top", {"start": v(19.05, -0.63) * mm, "end": v(19.05, 0.64) * mm});
            skLineSegment(sketch, "E145.left", {"start": v(15.24, 0.64) * mm, "end": v(19.05, 0.64) * mm});
            skLineSegment(sketch, "E145.right", {"start": v(15.24, -0.63) * mm, "end": v(19.05, -0.63) * mm});
            skLineSegment(sketch, "E146.bottom", {"start": v(13.02, -13.92) * mm, "end": v(13.92, -13.02) * mm});
            skLineSegment(sketch, "E146.top", {"start": v(10.33, -11.23) * mm, "end": v(11.23, -10.33) * mm});
            skLineSegment(sketch, "E146.left", {"start": v(13.92, -13.02) * mm, "end": v(11.23, -10.33) * mm});
            skLineSegment(sketch, "E146.right", {"start": v(13.02, -13.92) * mm, "end": v(10.33, -11.23) * mm});
            skLineSegment(sketch, "E147.bottom", {"start": v(-0.63, -15.24) * mm, "end": v(0.63, -15.24) * mm});
            skLineSegment(sketch, "E147.top", {"start": v(-0.64, -19.05) * mm, "end": v(0.64, -19.05) * mm});
            skLineSegment(sketch, "E147.left", {"start": v(-0.63, -15.24) * mm, "end": v(-0.63, -19.05) * mm});
            skLineSegment(sketch, "E147.right", {"start": v(0.64, -15.24) * mm, "end": v(0.64, -19.05) * mm});
            skLineSegment(sketch, "E148.bottom", {"start": v(-11.23, -10.33) * mm, "end": v(-10.33, -11.23) * mm});
            skLineSegment(sketch, "E148.top", {"start": v(-13.92, -13.02) * mm, "end": v(-13.02, -13.92) * mm});
            skLineSegment(sketch, "E148.left", {"start": v(-11.23, -10.33) * mm, "end": v(-13.92, -13.02) * mm});
            skLineSegment(sketch, "E148.right", {"start": v(-10.33, -11.23) * mm, "end": v(-13.02, -13.92) * mm});
            skSolve(sketch);
        }
        {
            var Q0;
            Q0 = qSketchRegion(id + "F37", true);
            extrude(context, id + "F38", {"entities" : qUnion([Q0]), "operationType" : NewBodyOperationType.ADD, "depth" : 1.27 * mm});
        }
        {
            var Q0;
            Q0=makeQuery(id+"F15.opRevolve","SWEPT_FACE",FACE,{"disambiguationData":[OSD([sQuery(id+"F14.wireOp",EDGE,"E41.bottom")])]});
            var sketch = newSketch(context, id + "F39", { "sketchPlane" : qUnion([Q0])});
            skLineSegment(sketch, "E149.bottom", {"start": v(-20.2, 19.3) * mm, "end": v(-19.3, 20.2) * mm});
            skLineSegment(sketch, "E149.top", {"start": v(-17.51, 16.61) * mm, "end": v(-16.61, 17.51) * mm});
            skLineSegment(sketch, "E149.left", {"start": v(-20.2, 19.3) * mm, "end": v(-17.51, 16.61) * mm});
            skLineSegment(sketch, "E149.right", {"start": v(-19.3, 20.2) * mm, "end": v(-16.61, 17.51) * mm});
            skLineSegment(sketch, "E150.bottom", {"start": v(-0.63, 27.94) * mm, "end": v(0.63, 27.94) * mm});
            skLineSegment(sketch, "E150.top", {"start": v(-0.63, 24.13) * mm, "end": v(0.63, 24.13) * mm});
            skLineSegment(sketch, "E150.left", {"start": v(-0.63, 27.94) * mm, "end": v(-0.63, 24.13) * mm});
            skLineSegment(sketch, "E150.right", {"start": v(0.64, 27.94) * mm, "end": v(0.64, 24.13) * mm});
            skLineSegment(sketch, "E151.bottom", {"start": v(19.3, 20.2) * mm, "end": v(20.2, 19.3) * mm});
            skLineSegment(sketch, "E151.top", {"start": v(16.61, 17.51) * mm, "end": v(17.51, 16.61) * mm});
            skLineSegment(sketch, "E151.left", {"start": v(19.3, 20.2) * mm, "end": v(16.61, 17.51) * mm});
            skLineSegment(sketch, "E151.right", {"start": v(20.2, 19.3) * mm, "end": v(17.51, 16.61) * mm});
            skLineSegment(sketch, "E152.bottom", {"start": v(24.13, -0.64) * mm, "end": v(24.13, 0.64) * mm});
            skLineSegment(sketch, "E152.top", {"start": v(27.94, -0.64) * mm, "end": v(27.94, 0.64) * mm});
            skLineSegment(sketch, "E152.left", {"start": v(24.13, 0.64) * mm, "end": v(27.94, 0.64) * mm});
            skLineSegment(sketch, "E152.right", {"start": v(24.13, -0.64) * mm, "end": v(27.94, -0.64) * mm});
            skLineSegment(sketch, "E153.bottom", {"start": v(19.3, -20.2) * mm, "end": v(20.2, -19.3) * mm});
            skLineSegment(sketch, "E153.top", {"start": v(16.61, -17.51) * mm, "end": v(17.51, -16.61) * mm});
            skLineSegment(sketch, "E153.left", {"start": v(20.2, -19.3) * mm, "end": v(17.51, -16.61) * mm});
            skLineSegment(sketch, "E153.right", {"start": v(19.3, -20.2) * mm, "end": v(16.61, -17.51) * mm});
            skLineSegment(sketch, "E154.bottom", {"start": v(-0.64, -24.13) * mm, "end": v(0.64, -24.13) * mm});
            skLineSegment(sketch, "E154.top", {"start": v(-0.64, -27.94) * mm, "end": v(0.64, -27.94) * mm});
            skLineSegment(sketch, "E154.left", {"start": v(-0.64, -24.13) * mm, "end": v(-0.64, -27.94) * mm});
            skLineSegment(sketch, "E154.right", {"start": v(0.63, -24.13) * mm, "end": v(0.63, -27.94) * mm});
            skLineSegment(sketch, "E155.bottom", {"start": v(-17.51, -16.61) * mm, "end": v(-16.61, -17.51) * mm});
            skLineSegment(sketch, "E155.top", {"start": v(-20.2, -19.3) * mm, "end": v(-19.3, -20.2) * mm});
            skLineSegment(sketch, "E155.left", {"start": v(-17.51, -16.61) * mm, "end": v(-20.2, -19.3) * mm});
            skLineSegment(sketch, "E155.right", {"start": v(-16.61, -17.51) * mm, "end": v(-19.3, -20.2) * mm});
            skLineSegment(sketch, "E156.bottom", {"start": v(-27.94, 0.63) * mm, "end": v(-24.13, 0.63) * mm});
            skLineSegment(sketch, "E156.top", {"start": v(-27.94, -0.63) * mm, "end": v(-24.13, -0.63) * mm});
            skLineSegment(sketch, "E156.left", {"start": v(-27.94, 0.63) * mm, "end": v(-27.94, -0.63) * mm});
            skLineSegment(sketch, "E156.right", {"start": v(-24.13, 0.63) * mm, "end": v(-24.13, -0.63) * mm});
            skSolve(sketch);
        }
        {
            var Q0;
            Q0 = qSketchRegion(id + "F39", true);
            extrude(context, id + "F40", {"entities" : qUnion([Q0]), "operationType" : NewBodyOperationType.ADD, "depth" : 1.27 * mm});
        }
        {
            var Q0;
            Q0=makeQuery(id+"F7.boolean.opBoolean","SPLIT",BODY,{"disambiguationData":[OD(0.0)],"derivedFrom":makeQuery(id+"F3.opRevolve","SWEPT_BODY",BODY,{"disambiguationData":[OSD([sQuery(id+"F2.wireOp",EDGE,"E8.top"),sQuery(id+"F2.wireOp",EDGE,"E8.left"),sQuery(id+"F2.wireOp",EDGE,"E9"),sQuery(id+"F2.wireOp",EDGE,"E10"),sQuery(id+"F2.wireOp",EDGE,"E12"),sQuery(id+"F2.wireOp",EDGE,"E13")])]})});
            deleteBodies(context, id + "F41", {"entities" : qUnion([Q0])});
        }
        {
            var Q0;
            Q0=makeQuery(id+"F1.opRevolve","SWEPT_BODY",BODY,{"disambiguationData":[OSD([sQuery(id+"F0.wireOp",EDGE,"E0"),sQuery(id+"F0.wireOp",EDGE,"E2"),sQuery(id+"F0.wireOp",EDGE,"E3"),sQuery(id+"F0.wireOp",EDGE,"E4"),sQuery(id+"F0.wireOp",EDGE,"E6"),sQuery(id+"F0.wireOp",EDGE,"E7")])]});
            var Q1;
            Q1=makeQuery(id+"F5.opRevolve","SWEPT_BODY",BODY,{"disambiguationData":[OSD([sQuery(id+"F4.wireOp",EDGE,"E14.bottom"),sQuery(id+"F4.wireOp",EDGE,"E14.top"),sQuery(id+"F4.wireOp",EDGE,"E14.left"),sQuery(id+"F4.wireOp",EDGE,"E14.right"),sQuery(id+"F4.wireOp",EDGE,"E15"),sQuery(id+"F4.wireOp",EDGE,"E16")])]});
            var Q2;
            Q2=makeQuery(id+"F7.boolean.opBoolean","SPLIT",BODY,{"disambiguationData":[OD(1.0)],"derivedFrom":makeQuery(id+"F3.opRevolve","SWEPT_BODY",BODY,{"disambiguationData":[OSD([sQuery(id+"F2.wireOp",EDGE,"E8.top"),sQuery(id+"F2.wireOp",EDGE,"E8.left"),sQuery(id+"F2.wireOp",EDGE,"E9"),sQuery(id+"F2.wireOp",EDGE,"E10"),sQuery(id+"F2.wireOp",EDGE,"E12"),sQuery(id+"F2.wireOp",EDGE,"E13")])]})});
            var Q3;
            Q3=makeQuery(id+"F11.opRevolve","SWEPT_BODY",BODY,{"disambiguationData":[OSD([sQuery(id+"F10.wireOp",EDGE,"E25"),sQuery(id+"F10.wireOp",EDGE,"E27"),sQuery(id+"F10.wireOp",EDGE,"E28"),sQuery(id+"F10.wireOp",EDGE,"E29"),sQuery(id+"F10.wireOp",EDGE,"E31"),sQuery(id+"F10.wireOp",EDGE,"E32")])]});
            var Q4;
            Q4=makeQuery(id+"F13.opRevolve","SWEPT_BODY",BODY,{"disambiguationData":[OSD([sQuery(id+"F12.wireOp",EDGE,"E33"),sQuery(id+"F12.wireOp",EDGE,"E35"),sQuery(id+"F12.wireOp",EDGE,"E36"),sQuery(id+"F12.wireOp",EDGE,"E37"),sQuery(id+"F12.wireOp",EDGE,"E39"),sQuery(id+"F12.wireOp",EDGE,"E40")])]});
            var Q5;
            Q5=makeQuery(id+"F15.opRevolve","SWEPT_BODY",BODY,{"disambiguationData":[OSD([sQuery(id+"F14.wireOp",EDGE,"E41.bottom"),sQuery(id+"F14.wireOp",EDGE,"E41.top"),sQuery(id+"F14.wireOp",EDGE,"E41.left"),sQuery(id+"F14.wireOp",EDGE,"E41.right")])]});
            var Q6;
            Q6=makeQuery(id+"F17.opRevolve","SWEPT_BODY",BODY,{"disambiguationData":[OSD([sQuery(id+"F16.wireOp",EDGE,"E42"),sQuery(id+"F16.wireOp",EDGE,"E44"),sQuery(id+"F16.wireOp",EDGE,"E45"),sQuery(id+"F16.wireOp",EDGE,"E46"),sQuery(id+"F16.wireOp",EDGE,"E48"),sQuery(id+"F16.wireOp",EDGE,"E49")])]});
            var Q7;
            Q7=makeQuery(id+"F19.opRevolve","SWEPT_BODY",BODY,{"disambiguationData":[OSD([sQuery(id+"F18.wireOp",EDGE,"E50"),sQuery(id+"F18.wireOp",EDGE,"E52"),sQuery(id+"F18.wireOp",EDGE,"E53"),sQuery(id+"F18.wireOp",EDGE,"E54"),sQuery(id+"F18.wireOp",EDGE,"E56"),sQuery(id+"F18.wireOp",EDGE,"E57")])]});
            var Q8;
            Q8=makeQuery(id+"F23.opRevolve","SWEPT_BODY",BODY,{"disambiguationData":[OSD([sQuery(id+"F22.wireOp",EDGE,"E66"),sQuery(id+"F22.wireOp",EDGE,"E67"),sQuery(id+"F22.wireOp",EDGE,"E68")])]});
            var Q9;
            Q9=makeQuery(id+"F25.opRevolve","SWEPT_BODY",BODY,{"disambiguationData":[OSD([sQuery(id+"F24.wireOp",EDGE,"E69"),sQuery(id+"F24.wireOp",EDGE,"E71"),sQuery(id+"F24.wireOp",EDGE,"E72"),sQuery(id+"F24.wireOp",EDGE,"E73"),sQuery(id+"F24.wireOp",EDGE,"E75"),sQuery(id+"F24.wireOp",EDGE,"E76")])]});
            var Q10;
            Q10=sQuery(id+"F26.wireOp",VERTEX,"E89.start");
            transform(context, id + "F42", {"entities" : qUnion([Q0, Q1, Q2, Q3, Q4, Q5, Q6, Q7, Q8, Q9]), "transformType" : TransformType.SCALE_UNIFORMLY, "scale" : 0.85, "makeCopy" : true, "scalePoint" : qUnion([Q10])});
        }
    });
